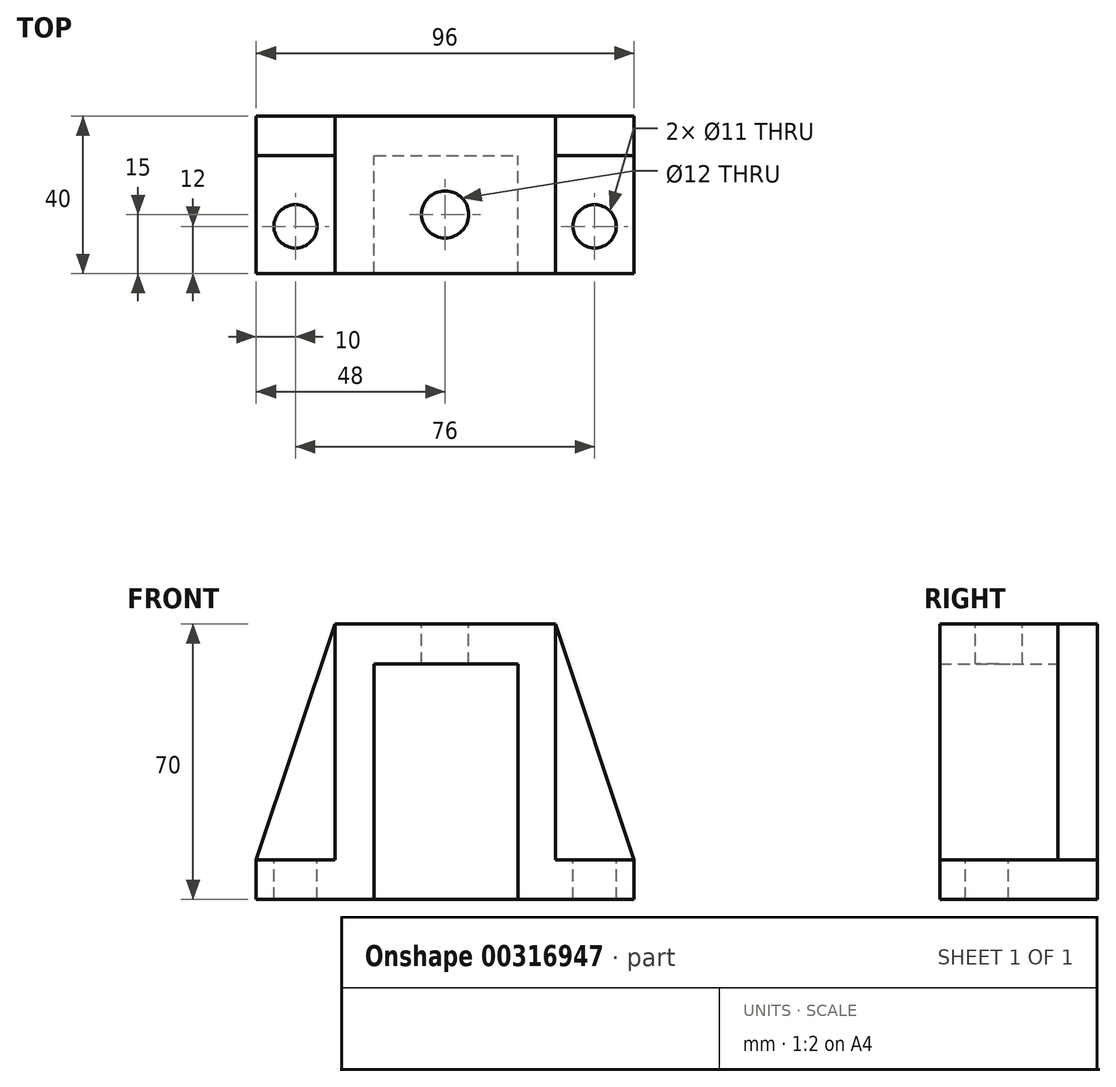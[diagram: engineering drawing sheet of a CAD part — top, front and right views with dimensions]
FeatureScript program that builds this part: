
annotation { "Feature Type Name" : "Feature", "Feature Type Description" : "" }
export const myFeature = defineFeature(function(context is Context, id is Id, definition is map)
    precondition{}
    {
        {
            var Q0;
            Q0=qCreatedBy(makeId("Front.planeOp"),FACE);
            var sketch = newSketch(context, id + "F0", { "sketchPlane" : qUnion([Q0])});
            skLineSegment(sketch, "E0", {"start": v(-48, 0) * mm, "end": v(48, 0) * mm});
            skLineSegment(sketch, "E1", {"start": v(48, 0) * mm, "end": v(48, 10) * mm});
            skLineSegment(sketch, "E2", {"start": v(48, 10) * mm, "end": v(28, 70) * mm});
            skLineSegment(sketch, "E3", {"start": v(28, 70) * mm, "end": v(-28, 70) * mm});
            skLineSegment(sketch, "E4", {"start": v(-28, 70) * mm, "end": v(-48, 10) * mm});
            skLineSegment(sketch, "E5", {"start": v(-48, 10) * mm, "end": v(-48, 0) * mm});
            skSolve(sketch);
        }
        {
            var Q0;
            Q0=makeQuery(id+"F0.imprint","IMPRINT",FACE,{"disambiguationData":[TD([[makeQuery(id+"F0.imprint","IMPRINT",EDGE,{"derivedFrom":sQuery(id+"F0.wireOp",EDGE,"E0")}),1.0]])]});
            extrude(context, id + "F1", {"entities" : qUnion([Q0]), "depth" : 10 * mm});
        }
        {
            var Q0;
            Q0=makeQuery(id+"F1.opExtrude","CAP_FACE",FACE,{"disambiguationData":[OSD([sQuery(id+"F0.wireOp",EDGE,"E0"),sQuery(id+"F0.wireOp",EDGE,"E1"),sQuery(id+"F0.wireOp",EDGE,"E2"),sQuery(id+"F0.wireOp",EDGE,"E3"),sQuery(id+"F0.wireOp",EDGE,"E4"),sQuery(id+"F0.wireOp",EDGE,"E5")])],"isStart":false});
            var sketch = newSketch(context, id + "F2", { "sketchPlane" : qUnion([Q0])});
            skLineSegment(sketch, "E6", {"start": v(-48, 10) * mm, "end": v(-28, 10) * mm});
            skLineSegment(sketch, "E7", {"start": v(-28, 10) * mm, "end": v(-28, 70) * mm});
            skLineSegment(sketch, "E8", {"start": v(-28, 70) * mm, "end": v(28, 70) * mm});
            skLineSegment(sketch, "E9", {"start": v(28, 70) * mm, "end": v(28, 10) * mm});
            skLineSegment(sketch, "E10", {"start": v(28, 10) * mm, "end": v(48, 10) * mm});
            skLineSegment(sketch, "E11", {"start": v(48, 10) * mm, "end": v(48, 0) * mm});
            skLineSegment(sketch, "E12", {"start": v(48, 0) * mm, "end": v(18.5, 0) * mm});
            skLineSegment(sketch, "E13", {"start": v(18.5, 0) * mm, "end": v(18.5, 59.78) * mm});
            skLineSegment(sketch, "E14", {"start": v(18.5, 59.78) * mm, "end": v(-18, 59.78) * mm});
            skLineSegment(sketch, "E15", {"start": v(-18, 59.78) * mm, "end": v(-18, 0) * mm});
            skLineSegment(sketch, "E16", {"start": v(-18, 0) * mm, "end": v(-48, 0) * mm});
            skLineSegment(sketch, "E17", {"start": v(-48, 0) * mm, "end": v(-48, 10) * mm});
            skSolve(sketch);
        }
        {
            var Q0;
            Q0=makeQuery(id+"F2.imprint","IMPRINT",FACE,{"disambiguationData":[TD([[makeQuery(id+"F2.imprint","IMPRINT",EDGE,{"derivedFrom":sQuery(id+"F2.wireOp",EDGE,"E6")}),-1.0]])]});
            extrude(context, id + "F3", {"entities" : qUnion([Q0]), "operationType" : NewBodyOperationType.ADD, "depth" : 30 * mm});
        }
        {
            var Q0;
            Q0=makeQuery(id+"F3.opExtrude","SWEPT_FACE",FACE,{"disambiguationData":[OSD([sQuery(id+"F2.wireOp",EDGE,"E6")])]});
            var sketch = newSketch(context, id + "F4", { "sketchPlane" : qUnion([Q0])});
            skCircle(sketch, "E18", {"center": v(-38, -28) * mm, "radius": 5.5 * mm});
            skSolve(sketch);
        }
        {
            var Q0;
            Q0=makeQuery(id+"F4.imprint","IMPRINT",FACE,{"disambiguationData":[TD([[makeQuery(id+"F4.imprint","IMPRINT",EDGE,{"derivedFrom":sQuery(id+"F4.wireOp",EDGE,"E18")}),1.0]])]});
            extrude(context, id + "F5", {"entities" : qUnion([Q0]), "operationType" : NewBodyOperationType.REMOVE, "oppositeDirection" : true, "depth" : 25 * mm});
        }
        {
            var Q0;
            Q0=makeQuery(id+"F3.boolean.opBoolean","MERGE",FACE,{"derivedFrom":[makeQuery(id+"F1.opExtrude","SWEPT_FACE",FACE,{"disambiguationData":[OSD([sQuery(id+"F0.wireOp",EDGE,"E3")])]}),makeQuery(id+"F3.opExtrude","SWEPT_FACE",FACE,{"disambiguationData":[OSD([sQuery(id+"F2.wireOp",EDGE,"E8")])]})]});
            var sketch = newSketch(context, id + "F6", { "sketchPlane" : qUnion([Q0])});
            skCircle(sketch, "E19", {"center": v(0, -25) * mm, "radius": 6 * mm});
            skSolve(sketch);
        }
        {
            var Q0;
            Q0=makeQuery(id+"F6.imprint","IMPRINT",FACE,{"disambiguationData":[TD([[makeQuery(id+"F6.imprint","IMPRINT",EDGE,{"derivedFrom":sQuery(id+"F6.wireOp",EDGE,"E19")}),1.0]])]});
            extrude(context, id + "F7", {"entities" : qUnion([Q0]), "operationType" : NewBodyOperationType.REMOVE, "oppositeDirection" : true, "depth" : 25 * mm});
        }
        {
            var Q0;
            Q0=makeQuery(id+"F3.opExtrude","SWEPT_FACE",FACE,{"disambiguationData":[OSD([sQuery(id+"F2.wireOp",EDGE,"E10")])]});
            var sketch = newSketch(context, id + "F8", { "sketchPlane" : qUnion([Q0])});
            skCircle(sketch, "E20", {"center": v(38, -28) * mm, "radius": 5.5 * mm});
            skSolve(sketch);
        }
        {
            var Q0;
            Q0=makeQuery(id+"F8.imprint","IMPRINT",FACE,{"disambiguationData":[TD([[makeQuery(id+"F8.imprint","IMPRINT",EDGE,{"derivedFrom":sQuery(id+"F8.wireOp",EDGE,"E20")}),1.0]])]});
            extrude(context, id + "F9", {"entities" : qUnion([Q0]), "operationType" : NewBodyOperationType.REMOVE, "oppositeDirection" : true, "depth" : 25 * mm});
        }
    });
